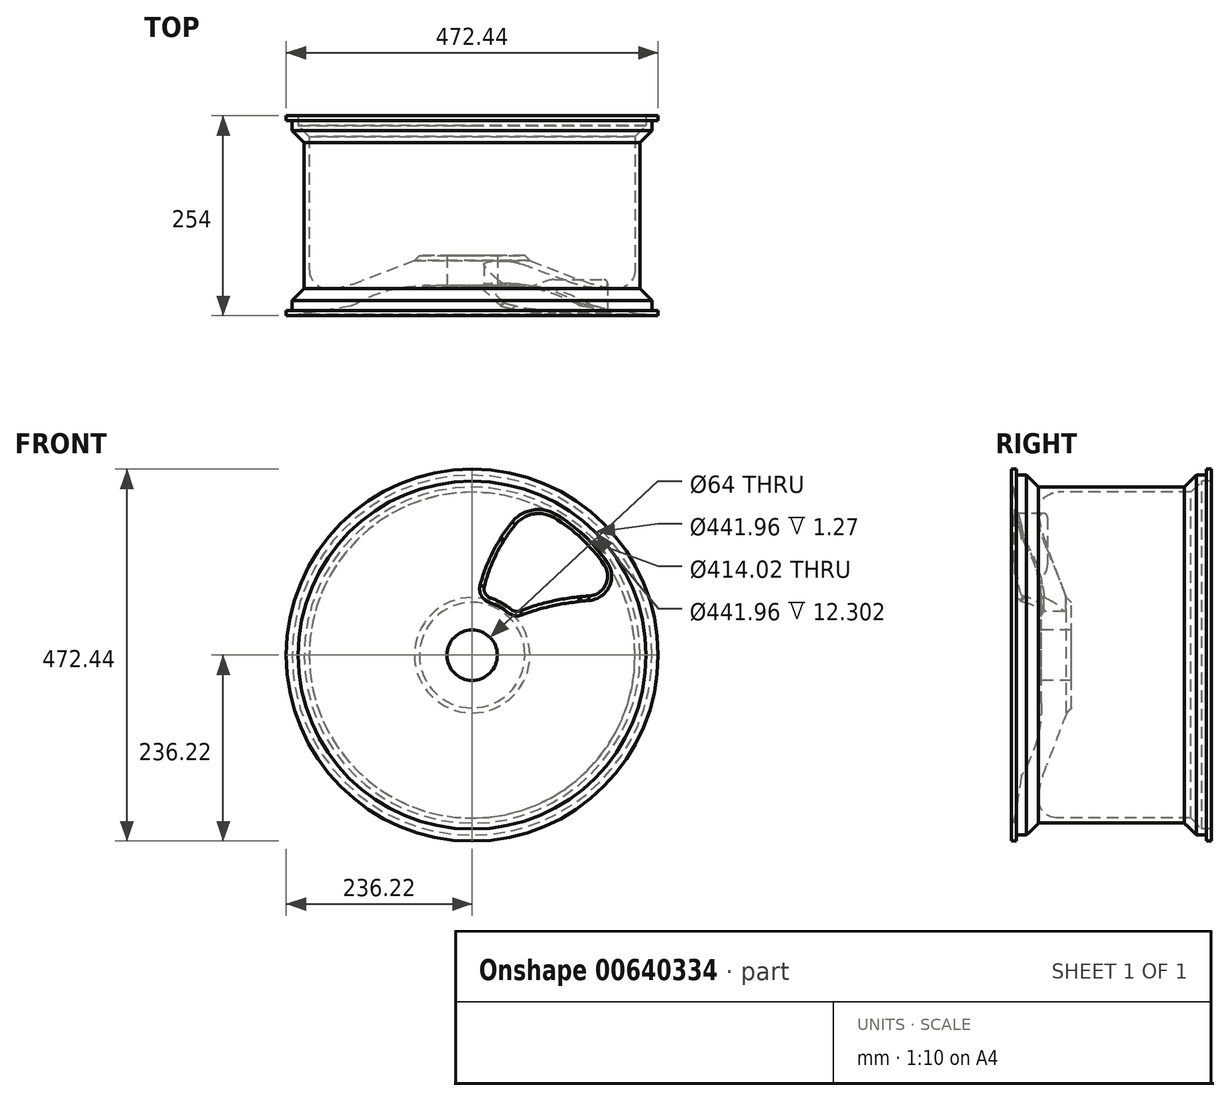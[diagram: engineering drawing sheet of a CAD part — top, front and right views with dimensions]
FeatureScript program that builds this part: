
annotation { "Feature Type Name" : "Feature", "Feature Type Description" : "" }
export const myFeature = defineFeature(function(context is Context, id is Id, definition is map)
    precondition{}
    {
        {
            var Q0;
            Q0=qCreatedBy(makeId("Right.planeOp"),FACE);
            var sketch = newSketch(context, id + "F0", { "sketchPlane" : qUnion([Q0])});
            skLineSegment(sketch, "E0", {"start": v(0, 0) * mm, "end": v(254, 0) * mm, "construction": true});
            skLineSegment(sketch, "E1", {"start": v(38.1, 32) * mm, "end": v(76.2, 32) * mm});
            skLineSegment(sketch, "E2", {"start": v(76.2, 32) * mm, "end": v(76.2, 67) * mm});
            skLineSegment(sketch, "E3", {"start": v(76.2, 67) * mm, "end": v(69.85, 73.35) * mm});
            skLineSegment(sketch, "E4", {"start": v(38.1, 32) * mm, "end": v(38.1, 61.35) * mm});
            skArc(sketch, "E5", {"start": v(38.1, 61.35) * mm, "mid": v(31.63, 108.61) * mm, "end": v(12.7, 152.4) * mm});
            skLineSegment(sketch, "E6", {"start": v(12.7, 152.4) * mm, "end": v(0, 228.6) * mm});
            skLineSegment(sketch, "E7", {"start": v(-20.5, 55) * mm, "end": v(125.52, 55) * mm, "construction": true});
            skLineSegment(sketch, "E8", {"start": v(0, 228.6) * mm, "end": v(70.76, 228.6) * mm, "construction": true});
            skLineSegment(sketch, "E9", {"start": v(0, 228.6) * mm, "end": v(0, 0) * mm, "construction": true});
            skLineSegment(sketch, "E10", {"start": v(69.85, 73.35) * mm, "end": v(44.45, 139.7) * mm});
            skArc(sketch, "E11", {"start": v(44.45, 139.7) * mm, "mid": v(33.1, 183.44) * mm, "end": v(31.75, 228.6) * mm});
            skLineSegment(sketch, "E12", {"start": v(0, 228.6) * mm, "end": v(31.75, 228.6) * mm});
            skSolve(sketch);
        }
        {
            var Q0;
            Q0 = qSketchRegion(id + "F0", true);
            var Q1;
            Q1=sQuery(id+"F0.wireOp",EDGE,"E0");
            revolve(context, id + "F1", {"entities" : qUnion([Q0]), "axis" : qUnion([Q1]), "revolveType" : RevolveType.FULL});
        }
        {
            var Q0;
            Q0=qCreatedBy(makeId("Front.planeOp"),FACE);
            var sketch = newSketch(context, id + "F2", { "sketchPlane" : qUnion([Q0])});
            skLineSegment(sketch, "E13", {"start": v(0, 0) * mm, "end": v(0, 225.46) * mm, "construction": true});
            skLineSegment(sketch, "E14", {"start": v(0, 0) * mm, "end": v(221.8, 72.07) * mm, "construction": true});
            skArc(sketch, "E15", {"start": v(167.6, 114.9) * mm, "mid": v(139, 148.22) * mm, "end": v(103.9, 174.62) * mm});
            skArc(sketch, "E16", {"start": v(48.7, 58.6) * mm, "mid": v(36.9, 66.67) * mm, "end": v(23.8, 72.4) * mm});
            skArc(sketch, "E17", {"start": v(54.9, 165.95) * mm, "mid": v(30.89, 128.92) * mm, "end": v(15.45, 87.58) * mm});
            skArc(sketch, "E18", {"start": v(148.15, 75.18) * mm, "mid": v(104.04, 69.16) * mm, "end": v(61.35, 56.5) * mm});
            skPoint(sketch, "E19.visualSharp", {"position": v(12.7, 75.13) * mm});
            skArc(sketch, "E19.filletArc", {"start": v(15.45, 87.58) * mm, "mid": v(16.63, 78.34) * mm, "end": v(23.8, 72.4) * mm});
            skPoint(sketch, "E20.visualSharp", {"position": v(54.12, 53.64) * mm});
            skArc(sketch, "E20.filletArc", {"start": v(48.7, 58.6) * mm, "mid": v(54.74, 55.84) * mm, "end": v(61.35, 56.5) * mm});
            skPoint(sketch, "E21.visualSharp", {"position": v(76.2, 188.37) * mm});
            skArc(sketch, "E21.filletArc", {"start": v(103.9, 174.62) * mm, "mid": v(77.79, 179.4) * mm, "end": v(54.9, 165.95) * mm});
            skPoint(sketch, "E22.visualSharp", {"position": v(188.95, 74.75) * mm});
            skArc(sketch, "E22.filletArc", {"start": v(148.15, 75.18) * mm, "mid": v(169.46, 89.37) * mm, "end": v(167.6, 114.9) * mm});
            skSolve(sketch);
        }
        {
            var Q0;
            {var subQ0=sQuery(id+"F0.wireOp",EDGE,"E5");var subQ2=sQuery(id+"F0.wireOp",EDGE,"E6");var subQ4=makeQuery(id+"F7.boolean.opBoolean","COPY",FACE,{"derivedFrom":makeQuery(id+"F7.opExtrude","SWEPT_FACE",FACE,{"disambiguationData":[OSD([sQuery(id+"F2.wireOp",EDGE,"E17")])]})});Q0=makeQuery(id+"F2RyRugOv9LZeXG_1.4.F7.boolean.opBoolean","SPLIT",EDGE,{"disambiguationData":[TD([subQ4])],"derivedFrom":makeQuery(id+"F2RyRugOv9LZeXG_1.3.F7.boolean.opBoolean","SPLIT",EDGE,{"disambiguationData":[TD([subQ4])],"derivedFrom":makeQuery(id+"F2RyRugOv9LZeXG_1.2.F7.boolean.opBoolean","SPLIT",EDGE,{"disambiguationData":[TD([subQ4])],"derivedFrom":makeQuery(id+"F2RyRugOv9LZeXG_1.1.F7.boolean.opBoolean","SPLIT",EDGE,{"disambiguationData":[TD([subQ4])],"derivedFrom":makeQuery(id+"F1.opRevolve","SWEPT_EDGE",EDGE,{"disambiguationData":[OSD([subQ0,subQ2])]})})})})});}
            var Q1;
            {var subQ0=sQuery(id+"F0.wireOp",EDGE,"E5");var subQ1=sQuery(id+"F0.wireOp",EDGE,"E6");Q1=makeQuery(id+"F2RyRugOv9LZeXG_1.1.F7.boolean.opBoolean","SPLIT",EDGE,{"disambiguationData":[TD([makeQuery(id+"F7.boolean.opBoolean","COPY",FACE,{"derivedFrom":makeQuery(id+"F7.opExtrude","SWEPT_FACE",FACE,{"disambiguationData":[OSD([sQuery(id+"F2.wireOp",EDGE,"E18")])]})})])],"derivedFrom":makeQuery(id+"F1.opRevolve","SWEPT_EDGE",EDGE,{"disambiguationData":[OSD([subQ0,subQ1])]})});}
            var Q2;
            {var subQ0=sQuery(id+"F0.wireOp",EDGE,"E5");var subQ2=makeQuery(id+"F2RyRugOv9LZeXG_1.1.F7.opExtrude","SWEPT_FACE",FACE,{"disambiguationData":[OSD([sQuery(id+"F2.wireOp",EDGE,"E18")])]});var subQ3=sQuery(id+"F0.wireOp",EDGE,"E6");var subQ5=sQuery(id+"F2.wireOp",EDGE,"E17");Q2=makeQuery(id+"F2RyRugOv9LZeXG_1.2.F7.boolean.opBoolean","SPLIT",EDGE,{"disambiguationData":[TD([makeQuery(id+"F2RyRugOv9LZeXG_1.1.F7.boolean.opBoolean","COPY",FACE,{"derivedFrom":subQ2})])],"derivedFrom":makeQuery(id+"F2RyRugOv9LZeXG_1.1.F7.boolean.opBoolean","SPLIT",EDGE,{"disambiguationData":[TD([makeQuery(id+"F7.boolean.opBoolean","COPY",FACE,{"derivedFrom":makeQuery(id+"F7.opExtrude","SWEPT_FACE",FACE,{"disambiguationData":[OSD([subQ5])]})})])],"derivedFrom":makeQuery(id+"F1.opRevolve","SWEPT_EDGE",EDGE,{"disambiguationData":[OSD([subQ0,subQ3])]})})});}
            var Q3;
            {var subQ0=sQuery(id+"F0.wireOp",EDGE,"E5");var subQ2=sQuery(id+"F0.wireOp",EDGE,"E6");var subQ4=sQuery(id+"F2.wireOp",EDGE,"E18");var subQ5=makeQuery(id+"F2RyRugOv9LZeXG_1.2.F7.opExtrude","SWEPT_FACE",FACE,{"disambiguationData":[OSD([subQ4])]});var subQ6=sQuery(id+"F2.wireOp",EDGE,"E17");var subQ7=makeQuery(id+"F7.boolean.opBoolean","COPY",FACE,{"derivedFrom":makeQuery(id+"F7.opExtrude","SWEPT_FACE",FACE,{"disambiguationData":[OSD([subQ6])]})});Q3=makeQuery(id+"F2RyRugOv9LZeXG_1.3.F7.boolean.opBoolean","SPLIT",EDGE,{"disambiguationData":[TD([makeQuery(id+"F2RyRugOv9LZeXG_1.2.F7.boolean.opBoolean","COPY",FACE,{"derivedFrom":subQ5})])],"derivedFrom":makeQuery(id+"F2RyRugOv9LZeXG_1.2.F7.boolean.opBoolean","SPLIT",EDGE,{"disambiguationData":[TD([subQ7])],"derivedFrom":makeQuery(id+"F2RyRugOv9LZeXG_1.1.F7.boolean.opBoolean","SPLIT",EDGE,{"disambiguationData":[TD([subQ7])],"derivedFrom":makeQuery(id+"F1.opRevolve","SWEPT_EDGE",EDGE,{"disambiguationData":[OSD([subQ0,subQ2])]})})})});}
            var Q4;
            {var subQ0=sQuery(id+"F0.wireOp",EDGE,"E5");var subQ2=sQuery(id+"F0.wireOp",EDGE,"E6");var subQ4=sQuery(id+"F2.wireOp",EDGE,"E17");var subQ5=sQuery(id+"F2.wireOp",EDGE,"E18");var subQ6=makeQuery(id+"F2RyRugOv9LZeXG_1.3.F7.opExtrude","SWEPT_FACE",FACE,{"disambiguationData":[OSD([subQ5])]});var subQ7=makeQuery(id+"F7.boolean.opBoolean","COPY",FACE,{"derivedFrom":makeQuery(id+"F7.opExtrude","SWEPT_FACE",FACE,{"disambiguationData":[OSD([subQ4])]})});Q4=makeQuery(id+"F2RyRugOv9LZeXG_1.4.F7.boolean.opBoolean","SPLIT",EDGE,{"disambiguationData":[TD([makeQuery(id+"F2RyRugOv9LZeXG_1.3.F7.boolean.opBoolean","COPY",FACE,{"derivedFrom":subQ6})])],"derivedFrom":makeQuery(id+"F2RyRugOv9LZeXG_1.3.F7.boolean.opBoolean","SPLIT",EDGE,{"disambiguationData":[TD([subQ7])],"derivedFrom":makeQuery(id+"F2RyRugOv9LZeXG_1.2.F7.boolean.opBoolean","SPLIT",EDGE,{"disambiguationData":[TD([subQ7])],"derivedFrom":makeQuery(id+"F2RyRugOv9LZeXG_1.1.F7.boolean.opBoolean","SPLIT",EDGE,{"disambiguationData":[TD([subQ7])],"derivedFrom":makeQuery(id+"F1.opRevolve","SWEPT_EDGE",EDGE,{"disambiguationData":[OSD([subQ0,subQ2])]})})})})});}
            fillet(context, id + "F3", {"entities" : qUnion([Q0, Q1, Q2, Q3, Q4]), "radius" : 7.62 * mm, "tangentPropagation" : true, "allowEdgeOverflow" : false});
        }
        {
            var Q0;
            Q0=qCreatedBy(makeId("Right.planeOp"),FACE);
            var sketch = newSketch(context, id + "F4", { "sketchPlane" : qUnion([Q0])});
            skLineSegment(sketch, "E23", {"start": v(0, 0) * mm, "end": v(254, 0) * mm, "construction": true});
            skLineSegment(sketch, "E24", {"start": v(264.9, 228.6) * mm, "end": v(-36.06, 228.6) * mm, "construction": true});
            skLineSegment(sketch, "E25", {"start": v(247.65, 236.22) * mm, "end": v(247.65, 228.6) * mm});
            skLineSegment(sketch, "E26", {"start": v(247.65, 228.6) * mm, "end": v(234.95, 228.6) * mm});
            skLineSegment(sketch, "E27", {"start": v(234.95, 228.6) * mm, "end": v(219.7, 213.36) * mm});
            skLineSegment(sketch, "E28", {"start": v(219.7, 213.36) * mm, "end": v(34.3, 213.36) * mm});
            skLineSegment(sketch, "E29", {"start": v(34.3, 213.36) * mm, "end": v(19.05, 228.6) * mm});
            skLineSegment(sketch, "E30", {"start": v(19.05, 228.6) * mm, "end": v(6.35, 228.6) * mm});
            skLineSegment(sketch, "E31", {"start": v(6.35, 228.6) * mm, "end": v(6.35, 236.22) * mm});
            skLineSegment(sketch, "E32", {"start": v(6.35, 236.22) * mm, "end": v(0, 236.22) * mm});
            skLineSegment(sketch, "E33", {"start": v(0, 236.22) * mm, "end": v(0, 220.98) * mm});
            skLineSegment(sketch, "E34", {"start": v(0, 220.98) * mm, "end": v(12.3, 220.98) * mm});
            skLineSegment(sketch, "E35", {"start": v(12.3, 220.98) * mm, "end": v(26.27, 207.01) * mm});
            skLineSegment(sketch, "E36", {"start": v(26.27, 207.01) * mm, "end": v(227.73, 207.01) * mm});
            skLineSegment(sketch, "E37", {"start": v(227.73, 207.01) * mm, "end": v(241.7, 220.98) * mm});
            skLineSegment(sketch, "E38", {"start": v(241.7, 220.98) * mm, "end": v(254, 220.98) * mm});
            skLineSegment(sketch, "E39", {"start": v(254, 220.98) * mm, "end": v(254, 236.22) * mm});
            skLineSegment(sketch, "E40", {"start": v(254, 236.22) * mm, "end": v(247.65, 236.22) * mm});
            skLineSegment(sketch, "E41", {"start": v(127, 213.36) * mm, "end": v(127, 207.01) * mm, "construction": true});
            skSolve(sketch);
        }
        {
            var Q0;
            Q0 = qSketchRegion(id + "F4", true);
            var Q1;
            Q1=sQuery(id+"F4.wireOp",EDGE,"E23");
            revolve(context, id + "F5", {"operationType" : NewBodyOperationType.ADD, "entities" : qUnion([Q0]), "axis" : qUnion([Q1]), "revolveType" : RevolveType.FULL});
        }
        {
            var Q0;
            Q0=makeQuery(id+"F5.boolean.opBoolean","INTERSECT",EDGE,{"derivedFrom":[makeQuery(id+"F1.opRevolve","SWEPT_FACE",FACE,{"disambiguationData":[OSD([sQuery(id+"F0.wireOp",EDGE,"E11")])]}),makeQuery(id+"F5.opRevolve","SWEPT_FACE",FACE,{"disambiguationData":[OSD([sQuery(id+"F4.wireOp",EDGE,"E36")])]})]});
            fillet(context, id + "F6", {"entities" : qUnion([Q0]), "radius" : 25.4 * mm, "tangentPropagation" : true, "allowEdgeOverflow" : false});
        }
        {
            var Q0;
            Q0 = qSketchRegion(id + "F2", true);
            extrude(context, id + "F7", {"entities" : qUnion([Q0]), "operationType" : NewBodyOperationType.REMOVE, "endBound" : BoundingType.THROUGH_ALL, "oppositeDirection" : true, "depth" : 25.4 * mm, "offsetDistance" : 25.4 * mm});
        }
        {
            var Q0;
            Q0=makeQuery(id+"F2RyRugOv9LZeXG_1.4.F7.boolean.opBoolean","INTERSECT",EDGE,{"derivedFrom":[makeQuery(id+"F1.opRevolve","SWEPT_FACE",FACE,{"disambiguationData":[OSD([sQuery(id+"F0.wireOp",EDGE,"E5")])]}),makeQuery(id+"F2RyRugOv9LZeXG_1.4.F7.opExtrude","SWEPT_FACE",FACE,{"disambiguationData":[OSD([sQuery(id+"F2.wireOp",EDGE,"E18")])]})]});
            var Q1;
            Q1=makeQuery(id+"F7.boolean.opBoolean","INTERSECT",EDGE,{"derivedFrom":[makeQuery(id+"F1.opRevolve","SWEPT_FACE",FACE,{"disambiguationData":[OSD([sQuery(id+"F0.wireOp",EDGE,"E5")])]}),makeQuery(id+"F7.opExtrude","SWEPT_FACE",FACE,{"disambiguationData":[OSD([sQuery(id+"F2.wireOp",EDGE,"E17")])]})]});
            var Q2;
            Q2=makeQuery(id+"F2RyRugOv9LZeXG_1.1.F7.boolean.opBoolean","INTERSECT",EDGE,{"derivedFrom":[makeQuery(id+"F1.opRevolve","SWEPT_FACE",FACE,{"disambiguationData":[OSD([sQuery(id+"F0.wireOp",EDGE,"E5")])]}),makeQuery(id+"F2RyRugOv9LZeXG_1.1.F7.opExtrude","SWEPT_FACE",FACE,{"disambiguationData":[OSD([sQuery(id+"F2.wireOp",EDGE,"E17")])]})]});
            var Q3;
            Q3=makeQuery(id+"F2RyRugOv9LZeXG_1.2.F7.boolean.opBoolean","INTERSECT",EDGE,{"derivedFrom":[makeQuery(id+"F1.opRevolve","SWEPT_FACE",FACE,{"disambiguationData":[OSD([sQuery(id+"F0.wireOp",EDGE,"E5")])]}),makeQuery(id+"F2RyRugOv9LZeXG_1.2.F7.opExtrude","SWEPT_FACE",FACE,{"disambiguationData":[OSD([sQuery(id+"F2.wireOp",EDGE,"E17")])]})]});
            var Q4;
            Q4=makeQuery(id+"F2RyRugOv9LZeXG_1.3.F7.boolean.opBoolean","INTERSECT",EDGE,{"derivedFrom":[makeQuery(id+"F1.opRevolve","SWEPT_FACE",FACE,{"disambiguationData":[OSD([sQuery(id+"F0.wireOp",EDGE,"E5")])]}),makeQuery(id+"F2RyRugOv9LZeXG_1.3.F7.opExtrude","SWEPT_FACE",FACE,{"disambiguationData":[OSD([sQuery(id+"F2.wireOp",EDGE,"E17")])]})]});
            chamfer(context, id + "F8", {"entities" : qUnion([Q0, Q1, Q2, Q3, Q4]), "chamferType" : ChamferType.TWO_OFFSETS, "width1" : 2.54 * mm, "oppositeDirection" : false, "width2" : 5.08 * mm, "tangentPropagation" : true});
        }
        {
            var Q0;
            Q0=qCreatedBy(makeId("Right.planeOp"),FACE);
            var sketch = newSketch(context, id + "F9", { "sketchPlane" : qUnion([Q0])});
            skLineSegment(sketch, "E42", {"start": v(34.3, 213.36) * mm, "end": v(34.3, 231.79) * mm});
            skLineSegment(sketch, "E43", {"start": v(34.3, 231.79) * mm, "end": v(15.86, 231.79) * mm});
            skLineSegment(sketch, "E44.0", {"start": v(34.3, 213.36) * mm, "end": v(15.86, 231.79) * mm});
            skPoint(sketch, "E45.orphan", {"position": v(19.05, 228.6) * mm});
            skLineSegment(sketch, "E46.0", {"start": v(0, 0) * mm, "end": v(254, 0) * mm, "construction": true});
            skSolve(sketch);
        }
        {
            var Q0;
            Q0 = qSketchRegion(id + "F9", true);
            var Q1;
            Q1=sQuery(id+"F9.wireOp",EDGE,"E46.0");
            revolve(context, id + "F10", {"operationType" : NewBodyOperationType.REMOVE, "entities" : qUnion([Q0]), "axis" : qUnion([Q1]), "revolveType" : RevolveType.FULL, "oppositeDirection" : true});
        }
    });
